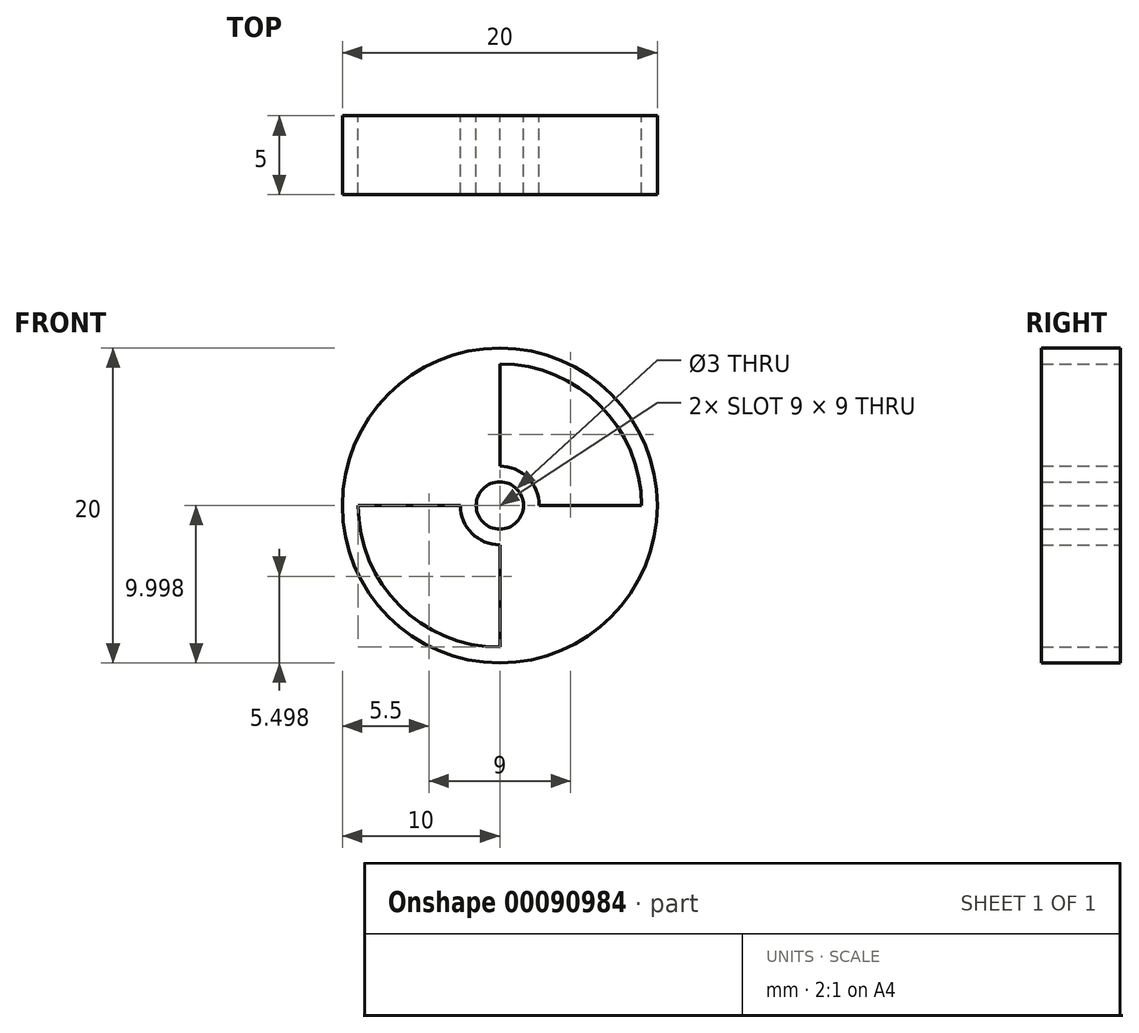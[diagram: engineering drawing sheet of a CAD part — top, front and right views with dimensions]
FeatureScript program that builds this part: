
annotation { "Feature Type Name" : "Feature", "Feature Type Description" : "" }
export const myFeature = defineFeature(function(context is Context, id is Id, definition is map)
    precondition{}
    {
        {
            var Q0;
            Q0=qCreatedBy(makeId("Front.planeOp"),FACE);
            var sketch = newSketch(context, id + "F0", { "sketchPlane" : qUnion([Q0])});
            skCircle(sketch, "E0", {"center": v(-28.45, 11.88) * mm, "radius": 10 * mm});
            skCircle(sketch, "E1", {"center": v(-28.45, 11.88) * mm, "radius": 1.5 * mm});
            skArc(sketch, "E2.0", {"start": v(-37.45, 11.88) * mm, "mid": v(-34.81, 5.51) * mm, "end": v(-28.45, 2.88) * mm});
            skArc(sketch, "E3.0", {"start": v(-30.95, 11.88) * mm, "mid": v(-30.22, 10.11) * mm, "end": v(-28.45, 9.38) * mm});
            skLineSegment(sketch, "E4", {"start": v(-28.45, 14.38) * mm, "end": v(-28.45, 20.88) * mm});
            skLineSegment(sketch, "E5", {"start": v(-28.45, 9.38) * mm, "end": v(-28.45, 2.88) * mm});
            skLineSegment(sketch, "E6", {"start": v(-25.95, 11.88) * mm, "end": v(-19.45, 11.88) * mm});
            skLineSegment(sketch, "E7", {"start": v(-30.95, 11.88) * mm, "end": v(-37.45, 11.88) * mm});
            skArc(sketch, "E8.trimOffspring", {"start": v(-25.95, 11.88) * mm, "mid": v(-26.68, 13.65) * mm, "end": v(-28.45, 14.38) * mm});
            skArc(sketch, "E9.trimOffspring", {"start": v(-19.45, 11.88) * mm, "mid": v(-22.09, 18.24) * mm, "end": v(-28.45, 20.88) * mm});
            skSolve(sketch);
        }
        {
            var Q0;
            Q0=makeQuery(id+"F0.imprint","IMPRINT",FACE,{"disambiguationData":[TD([[makeQuery(id+"F0.imprint","IMPRINT",EDGE,{"derivedFrom":sQuery(id+"F0.wireOp",EDGE,"E0")}),1.0]])]});
            extrude(context, id + "F1", {"entities" : qUnion([Q0]), "depth" : 5 * mm});
        }
    });
